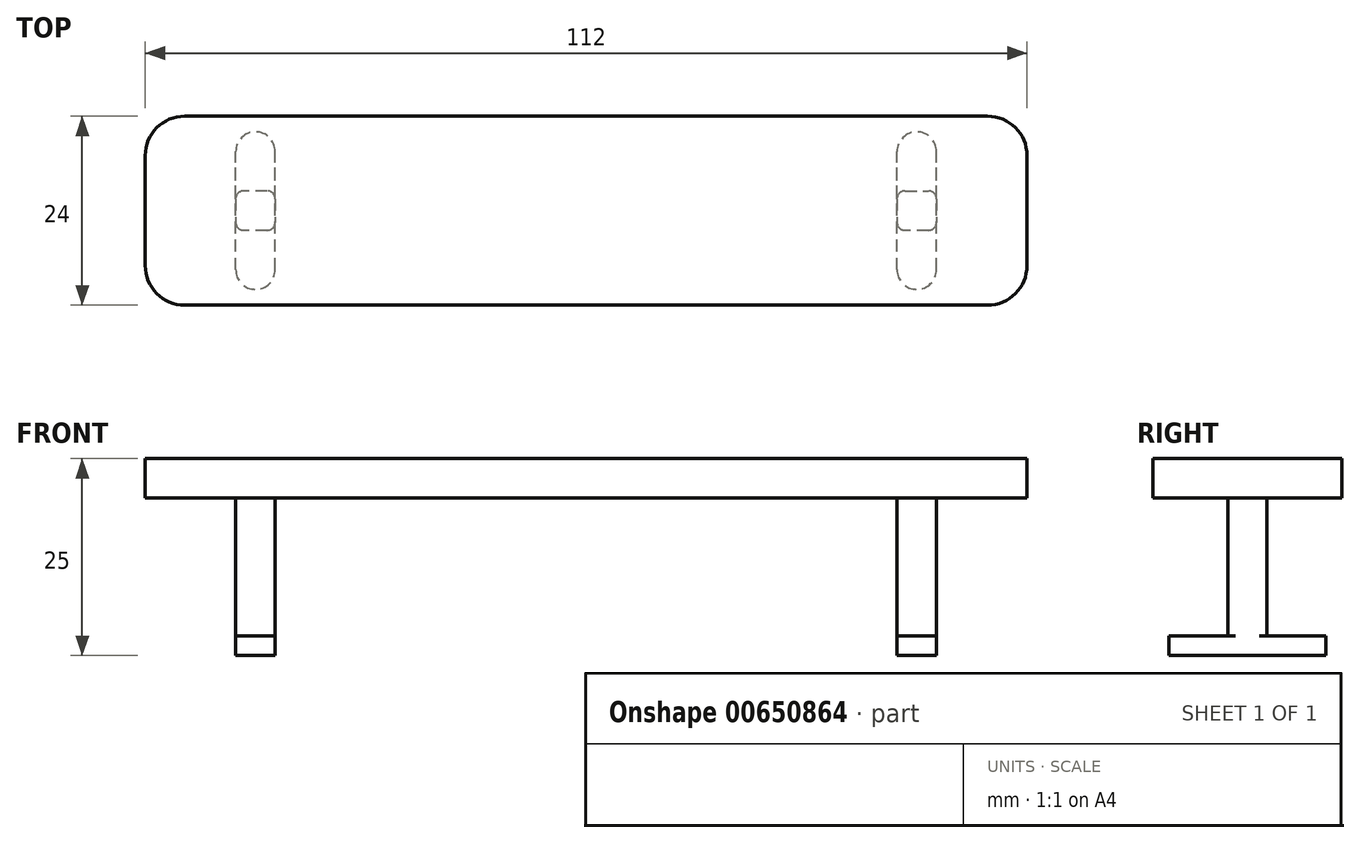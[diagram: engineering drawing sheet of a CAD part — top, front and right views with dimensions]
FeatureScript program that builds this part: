
annotation { "Feature Type Name" : "Feature", "Feature Type Description" : "" }
export const myFeature = defineFeature(function(context is Context, id is Id, definition is map)
    precondition{}
    {
        {
            var Q0;
            Q0=qCreatedBy(makeId("Top.planeOp"),FACE);
            var sketch = newSketch(context, id + "F0", { "sketchPlane" : qUnion([Q0])});
            skLineSegment(sketch, "E0.bottom", {"start": v(56, 12) * mm, "end": v(-56, 12) * mm});
            skLineSegment(sketch, "E0.top", {"start": v(56, -12) * mm, "end": v(-56, -12) * mm});
            skLineSegment(sketch, "E0.left", {"start": v(56, 12) * mm, "end": v(56, -12) * mm});
            skLineSegment(sketch, "E0.right", {"start": v(-56, 12) * mm, "end": v(-56, -12) * mm});
            skPoint(sketch, "E0.middle", {"position": v(0, 0) * mm});
            skLineSegment(sketch, "E1", {"start": v(-56, 0) * mm, "end": v(56, 0) * mm});
            skPoint(sketch, "E1.startSnap0", {"position": v(-56, 0) * mm});
            skLineSegment(sketch, "E2", {"start": v(0, 0) * mm, "end": v(-56, 0) * mm});
            skLineSegment(sketch, "E3", {"start": v(0, 0) * mm, "end": v(56, 0) * mm});
            skPoint(sketch, "E4", {"position": v(-28, 0) * mm});
            skPoint(sketch, "E5", {"position": v(28, 0) * mm});
            skLineSegment(sketch, "E6", {"start": v(-28, 0) * mm, "end": v(-56, 0) * mm});
            skLineSegment(sketch, "E7", {"start": v(28, 0) * mm, "end": v(56, 0) * mm});
            skPoint(sketch, "E8", {"position": v(-42, 0) * mm});
            skPoint(sketch, "E9", {"position": v(42, 0) * mm});
            skLineSegment(sketch, "E10.bottom", {"start": v(-39.5, -10) * mm, "end": v(-44.5, -10) * mm});
            skLineSegment(sketch, "E10.top", {"start": v(-39.5, 10) * mm, "end": v(-44.5, 10) * mm});
            skLineSegment(sketch, "E10.left", {"start": v(-39.5, -10) * mm, "end": v(-39.5, 10) * mm});
            skLineSegment(sketch, "E10.right", {"start": v(-44.5, -10) * mm, "end": v(-44.5, 10) * mm});
            skLineSegment(sketch, "E11.bottom", {"start": v(44.5, -10) * mm, "end": v(39.5, -10) * mm});
            skLineSegment(sketch, "E11.top", {"start": v(44.5, 10) * mm, "end": v(39.5, 10) * mm});
            skLineSegment(sketch, "E11.left", {"start": v(44.5, -10) * mm, "end": v(44.5, 10) * mm});
            skLineSegment(sketch, "E11.right", {"start": v(39.5, -10) * mm, "end": v(39.5, 10) * mm});
            skLineSegment(sketch, "E12", {"start": v(28, 0) * mm, "end": v(28, 2.5) * mm, "construction": true});
            skLineSegment(sketch, "E13", {"start": v(-28, 0) * mm, "end": v(-28, 2.5) * mm, "construction": true});
            skLineSegment(sketch, "E14", {"start": v(28, 2.5) * mm, "end": v(39.5, 2.5) * mm, "construction": true});
            skLineSegment(sketch, "E15", {"start": v(39.5, 2.5) * mm, "end": v(44.5, 2.5) * mm, "construction": true});
            skLineSegment(sketch, "E16", {"start": v(-28, 2.5) * mm, "end": v(-44.5, 2.5) * mm, "construction": true});
            skLineSegment(sketch, "E17", {"start": v(-28, 0) * mm, "end": v(-28, -2.5) * mm});
            skLineSegment(sketch, "E18", {"start": v(28, 0) * mm, "end": v(28, -2.5) * mm});
            skLineSegment(sketch, "E19", {"start": v(-28, -2.5) * mm, "end": v(-39.5, -2.5) * mm, "construction": true});
            skLineSegment(sketch, "E20", {"start": v(28, -2.5) * mm, "end": v(39.5, -2.5) * mm, "construction": true});
            skLineSegment(sketch, "E21", {"start": v(-44.5, 2.5) * mm, "end": v(-39.5, 2.5) * mm});
            skLineSegment(sketch, "E22", {"start": v(-44.5, -2.5) * mm, "end": v(-39.5, -2.5) * mm});
            skLineSegment(sketch, "E23", {"start": v(39.5, -2.5) * mm, "end": v(44.5, -2.5) * mm});
            skLineSegment(sketch, "E24", {"start": v(44.5, 2.5) * mm, "end": v(39.5, 2.5) * mm});
            skSolve(sketch);
        }
        {
            var Q0;
            {var subQ12=sQuery(id+"F0.wireOp",EDGE,"E0.bottom");Q0=makeQuery(id+"F0.imprint","IMPRINT",FACE,{"disambiguationData":[TD([[makeQuery(id+"F0.imprint","IMPRINT",EDGE,{"derivedFrom":subQ12}),1.0]])]});}
            var Q1;
            {var subQ16=sQuery(id+"F0.wireOp",EDGE,"E0.top");Q1=makeQuery(id+"F0.imprint","IMPRINT",FACE,{"disambiguationData":[TD([[makeQuery(id+"F0.imprint","IMPRINT",EDGE,{"derivedFrom":subQ16}),-1.0]])]});}
            extrude(context, id + "F1", {"entities" : qUnion([Q0, Q1]), "depth" : 25 * mm, "offsetDistance" : 25 * mm, "hasSecondDirection" : true, "secondDirectionOppositeDirection" : false, "secondDirectionDepth" : 20 * mm});
        }
        {
            var Q0;
            Q0=makeQuery(id+"F1.opExtrude","SWEPT_FACE",FACE,{"disambiguationData":[OSD([sQuery(id+"F0.wireOp",EDGE,"E11.right")])]});
            var Q1;
            Q1=makeQuery(id+"F1.opExtrude","SWEPT_FACE",FACE,{"disambiguationData":[OSD([sQuery(id+"F0.wireOp",EDGE,"E10.right")])]});
            extrude(context, id + "F2", {"entities" : qUnion([Q0, Q1]), "operationType" : NewBodyOperationType.ADD, "depth" : 5 * mm, "offsetDistance" : 25 * mm});
        }
        {
            var Q0;
            Q0=makeQuery(id+"F1.opExtrude","SWEPT_EDGE",EDGE,{"disambiguationData":[OSD([sQuery(id+"F0.wireOp",EDGE,"E0.top"),sQuery(id+"F0.wireOp",EDGE,"E0.left")])]});
            var Q1;
            Q1=makeQuery(id+"F1.opExtrude","SWEPT_EDGE",EDGE,{"disambiguationData":[OSD([sQuery(id+"F0.wireOp",EDGE,"E0.bottom"),sQuery(id+"F0.wireOp",EDGE,"E0.left")])]});
            var Q2;
            Q2=makeQuery(id+"F1.opExtrude","SWEPT_EDGE",EDGE,{"disambiguationData":[OSD([sQuery(id+"F0.wireOp",EDGE,"E0.top"),sQuery(id+"F0.wireOp",EDGE,"E0.right")])]});
            var Q3;
            Q3=makeQuery(id+"F1.opExtrude","SWEPT_EDGE",EDGE,{"disambiguationData":[OSD([sQuery(id+"F0.wireOp",EDGE,"E0.bottom"),sQuery(id+"F0.wireOp",EDGE,"E0.right")])]});
            fillet(context, id + "F3", {"entities" : qUnion([Q0, Q1, Q2, Q3]), "radius" : 5 * mm, "tangentPropagation" : true, "allowEdgeOverflow" : false});
        }
        {
            var Q0;
            {var subQ5=sQuery(id+"F0.wireOp",EDGE,"E22");Q0=makeQuery(id+"F0.imprint","IMPRINT",FACE,{"disambiguationData":[TD([[makeQuery(id+"F0.imprint","IMPRINT",EDGE,{"derivedFrom":subQ5}),1.0]])]});}
            var Q1;
            {var subQ5=sQuery(id+"F0.wireOp",EDGE,"E21");Q1=makeQuery(id+"F0.imprint","IMPRINT",FACE,{"disambiguationData":[TD([[makeQuery(id+"F0.imprint","IMPRINT",EDGE,{"derivedFrom":subQ5}),-1.0]])]});}
            var Q2;
            {var subQ5=sQuery(id+"F0.wireOp",EDGE,"E24");Q2=makeQuery(id+"F0.imprint","IMPRINT",FACE,{"disambiguationData":[TD([[makeQuery(id+"F0.imprint","IMPRINT",EDGE,{"derivedFrom":subQ5}),1.0]])]});}
            var Q3;
            {var subQ5=sQuery(id+"F0.wireOp",EDGE,"E23");Q3=makeQuery(id+"F0.imprint","IMPRINT",FACE,{"disambiguationData":[TD([[makeQuery(id+"F0.imprint","IMPRINT",EDGE,{"derivedFrom":subQ5}),1.0]])]});}
            extrude(context, id + "F4", {"entities" : qUnion([Q0, Q1, Q2, Q3]), "operationType" : NewBodyOperationType.ADD, "depth" : 25 * mm, "offsetDistance" : 25 * mm});
        }
        {
            var Q0;
            {var subQ0=sQuery(id+"F0.wireOp",EDGE,"E10.bottom");Q0=makeQuery(id+"F0.imprint","IMPRINT",FACE,{"disambiguationData":[TD([[makeQuery(id+"F0.imprint","IMPRINT",EDGE,{"derivedFrom":subQ0}),-1.0]])]});}
            var Q1;
            {var subQ0=sQuery(id+"F0.wireOp",EDGE,"E10.top");Q1=makeQuery(id+"F0.imprint","IMPRINT",FACE,{"disambiguationData":[TD([[makeQuery(id+"F0.imprint","IMPRINT",EDGE,{"derivedFrom":subQ0}),1.0]])]});}
            var Q2;
            {var subQ0=sQuery(id+"F0.wireOp",EDGE,"E11.top");Q2=makeQuery(id+"F0.imprint","IMPRINT",FACE,{"disambiguationData":[TD([[makeQuery(id+"F0.imprint","IMPRINT",EDGE,{"derivedFrom":subQ0}),1.0]])]});}
            var Q3;
            {var subQ0=sQuery(id+"F0.wireOp",EDGE,"E11.bottom");Q3=makeQuery(id+"F0.imprint","IMPRINT",FACE,{"disambiguationData":[TD([[makeQuery(id+"F0.imprint","IMPRINT",EDGE,{"derivedFrom":subQ0}),-1.0]])]});}
            extrude(context, id + "F5", {"entities" : qUnion([Q0, Q1, Q2, Q3]), "operationType" : NewBodyOperationType.ADD, "depth" : 2.5 * mm, "offsetDistance" : 25 * mm});
        }
        {
            var Q0;
            Q0=makeQuery(id+"F4.opExtrude","SWEPT_EDGE",EDGE,{"disambiguationData":[OSD([sQuery(id+"F0.wireOp",EDGE,"E11.left"),sQuery(id+"F0.wireOp",EDGE,"E23")])]});
            var Q1;
            Q1=makeQuery(id+"F4.opExtrude","SWEPT_EDGE",EDGE,{"disambiguationData":[OSD([sQuery(id+"F0.wireOp",EDGE,"E11.right"),sQuery(id+"F0.wireOp",EDGE,"E23")])]});
            var Q2;
            Q2=makeQuery(id+"F4.opExtrude","SWEPT_EDGE",EDGE,{"disambiguationData":[OSD([sQuery(id+"F0.wireOp",EDGE,"E11.left"),sQuery(id+"F0.wireOp",EDGE,"E24")])]});
            var Q3;
            Q3=makeQuery(id+"F4.opExtrude","SWEPT_EDGE",EDGE,{"disambiguationData":[OSD([sQuery(id+"F0.wireOp",EDGE,"E11.right"),sQuery(id+"F0.wireOp",EDGE,"E24")])]});
            var Q4;
            Q4=makeQuery(id+"F4.opExtrude","SWEPT_EDGE",EDGE,{"disambiguationData":[OSD([sQuery(id+"F0.wireOp",EDGE,"E10.left"),sQuery(id+"F0.wireOp",EDGE,"E21")])]});
            var Q5;
            Q5=makeQuery(id+"F4.opExtrude","SWEPT_EDGE",EDGE,{"disambiguationData":[OSD([sQuery(id+"F0.wireOp",EDGE,"E10.right"),sQuery(id+"F0.wireOp",EDGE,"E21")])]});
            var Q6;
            Q6=makeQuery(id+"F4.opExtrude","SWEPT_EDGE",EDGE,{"disambiguationData":[OSD([sQuery(id+"F0.wireOp",EDGE,"E10.right"),sQuery(id+"F0.wireOp",EDGE,"E22")])]});
            var Q7;
            Q7=makeQuery(id+"F4.opExtrude","SWEPT_EDGE",EDGE,{"disambiguationData":[OSD([sQuery(id+"F0.wireOp",EDGE,"E10.left"),sQuery(id+"F0.wireOp",EDGE,"E22")])]});
            fillet(context, id + "F6", {"entities" : qUnion([Q0, Q1, Q2, Q3, Q4, Q5, Q6, Q7]), "radius" : 1 * mm, "tangentPropagation" : true, "allowEdgeOverflow" : false});
        }
        {
            var Q0;
            Q0=makeQuery(id+"F5.opExtrude","SWEPT_EDGE",EDGE,{"disambiguationData":[OSD([sQuery(id+"F0.wireOp",EDGE,"E10.bottom"),sQuery(id+"F0.wireOp",EDGE,"E10.left")])]});
            var Q1;
            Q1=makeQuery(id+"F5.opExtrude","SWEPT_EDGE",EDGE,{"disambiguationData":[OSD([sQuery(id+"F0.wireOp",EDGE,"E10.bottom"),sQuery(id+"F0.wireOp",EDGE,"E10.right")])]});
            var Q2;
            Q2=makeQuery(id+"F5.opExtrude","SWEPT_EDGE",EDGE,{"disambiguationData":[OSD([sQuery(id+"F0.wireOp",EDGE,"E10.top"),sQuery(id+"F0.wireOp",EDGE,"E10.left")])]});
            var Q3;
            Q3=makeQuery(id+"F5.opExtrude","SWEPT_EDGE",EDGE,{"disambiguationData":[OSD([sQuery(id+"F0.wireOp",EDGE,"E10.top"),sQuery(id+"F0.wireOp",EDGE,"E10.right")])]});
            fillet(context, id + "F7", {"entities" : qUnion([Q0, Q1, Q2, Q3]), "radius" : 2.5 * mm, "tangentPropagation" : true, "allowEdgeOverflow" : false});
        }
        {
            var Q0;
            Q0=makeQuery(id+"F5.opExtrude","SWEPT_EDGE",EDGE,{"disambiguationData":[OSD([sQuery(id+"F0.wireOp",EDGE,"E11.bottom"),sQuery(id+"F0.wireOp",EDGE,"E11.right")])]});
            var Q1;
            Q1=makeQuery(id+"F5.opExtrude","SWEPT_EDGE",EDGE,{"disambiguationData":[OSD([sQuery(id+"F0.wireOp",EDGE,"E11.bottom"),sQuery(id+"F0.wireOp",EDGE,"E11.left")])]});
            var Q2;
            Q2=makeQuery(id+"F5.opExtrude","SWEPT_EDGE",EDGE,{"disambiguationData":[OSD([sQuery(id+"F0.wireOp",EDGE,"E11.top"),sQuery(id+"F0.wireOp",EDGE,"E11.left")])]});
            var Q3;
            Q3=makeQuery(id+"F5.opExtrude","SWEPT_EDGE",EDGE,{"disambiguationData":[OSD([sQuery(id+"F0.wireOp",EDGE,"E11.top"),sQuery(id+"F0.wireOp",EDGE,"E11.right")])]});
            fillet(context, id + "F8", {"entities" : qUnion([Q0, Q1, Q2, Q3]), "radius" : 2.5 * mm, "tangentPropagation" : true, "allowEdgeOverflow" : false});
        }
    });
